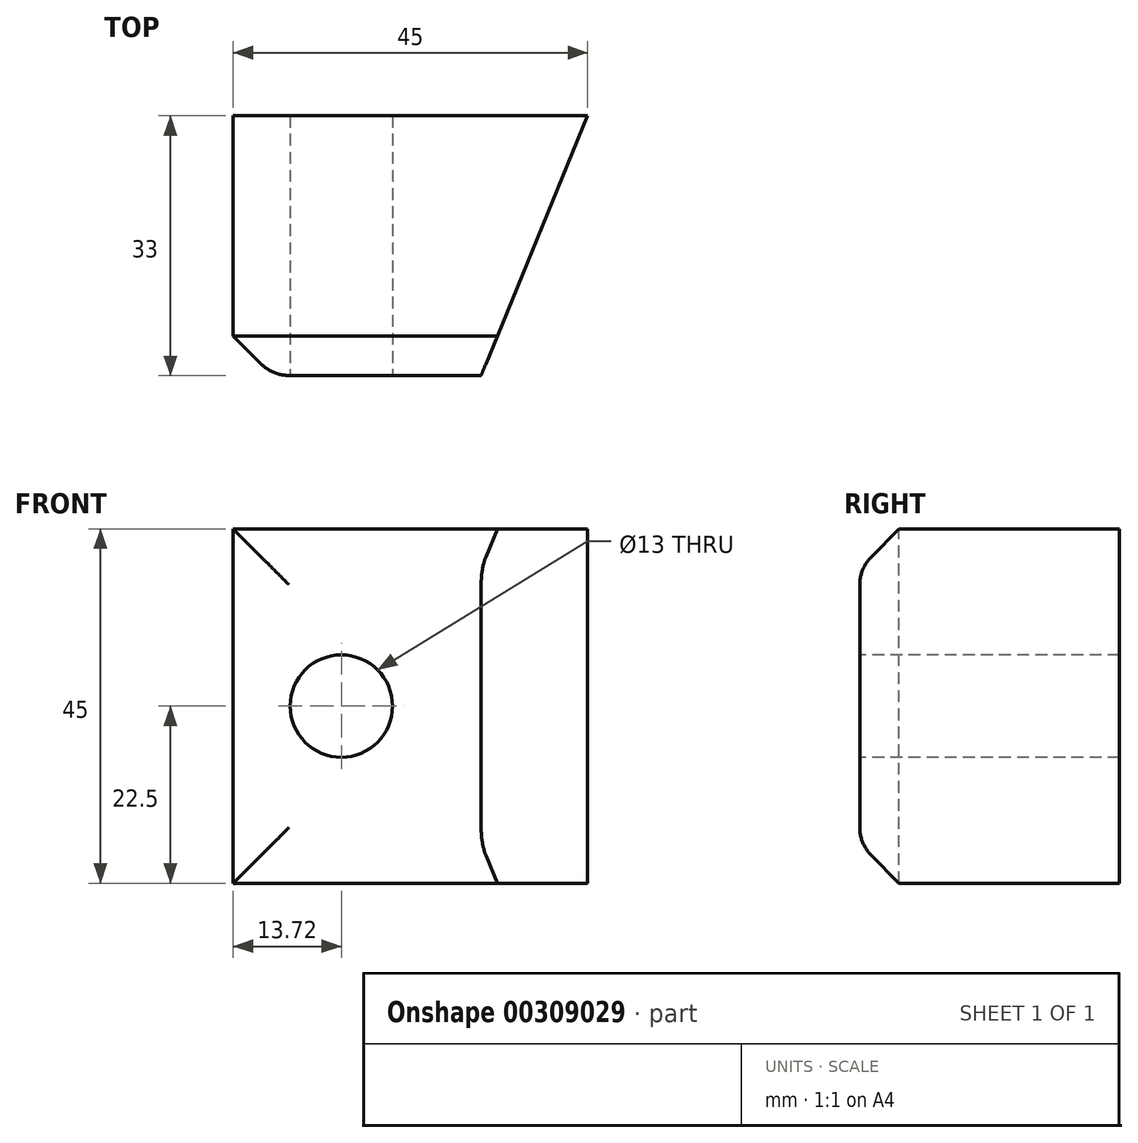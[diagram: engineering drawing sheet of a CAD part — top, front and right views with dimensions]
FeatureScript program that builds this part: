
annotation { "Feature Type Name" : "Feature", "Feature Type Description" : "" }
export const myFeature = defineFeature(function(context is Context, id is Id, definition is map)
    precondition{}
    {
        {
            var Q0;
            Q0=qCreatedBy(makeId("Front.planeOp"),FACE);
            var sketch = newSketch(context, id + "F0", { "sketchPlane" : qUnion([Q0])});
            skLineSegment(sketch, "E0.bottom", {"start": v(22.5, 22.5) * mm, "end": v(-22.5, 22.5) * mm});
            skLineSegment(sketch, "E0.top", {"start": v(22.5, -22.5) * mm, "end": v(-22.5, -22.5) * mm});
            skLineSegment(sketch, "E0.left", {"start": v(22.5, 22.5) * mm, "end": v(22.5, -22.5) * mm});
            skLineSegment(sketch, "E0.right", {"start": v(-22.5, 22.5) * mm, "end": v(-22.5, -22.5) * mm});
            skPoint(sketch, "E0.middle", {"position": v(0, 0) * mm});
            skSolve(sketch);
        }
        {
            var Q0;
            Q0 = qSketchRegion(id + "F0", true);
            extrude(context, id + "F1", {"entities" : qUnion([Q0]), "depth" : 33 * mm, "offsetDistance" : 25 * mm});
        }
        {
            var Q0;
            Q0=makeQuery(id+"F1.opExtrude","SWEPT_FACE",FACE,{"disambiguationData":[OSD([sQuery(id+"F0.wireOp",EDGE,"E0.bottom")])]});
            var sketch = newSketch(context, id + "F2", { "sketchPlane" : qUnion([Q0])});
            skLineSegment(sketch, "E1", {"start": v(22.5, 0) * mm, "end": v(8.98, -33) * mm});
            skLineSegment(sketch, "E2", {"start": v(8.98, -33) * mm, "end": v(22.5, -33) * mm});
            skLineSegment(sketch, "E3", {"start": v(22.5, -33) * mm, "end": v(22.5, 0) * mm});
            skSolve(sketch);
        }
        {
            var Q0;
            Q0 = qSketchRegion(id + "F2", true);
            extrude(context, id + "F3", {"entities" : qUnion([Q0]), "operationType" : NewBodyOperationType.REMOVE, "oppositeDirection" : true, "depth" : 55.8 * mm, "offsetDistance" : 25 * mm});
        }
        {
            var Q0;
            Q0=makeQuery(id+"F1.opExtrude","CAP_FACE",FACE,{"disambiguationData":[OSD([sQuery(id+"F0.wireOp",EDGE,"E0.bottom"),sQuery(id+"F0.wireOp",EDGE,"E0.top"),sQuery(id+"F0.wireOp",EDGE,"E0.left"),sQuery(id+"F0.wireOp",EDGE,"E0.right")])],"isStart":false});
            var sketch = newSketch(context, id + "F4", { "sketchPlane" : qUnion([Q0])});
            skCircle(sketch, "E4", {"center": v(-8.78, 0) * mm, "radius": 6.5 * mm});
            skSolve(sketch);
        }
        {
            var Q0;
            Q0 = qSketchRegion(id + "F4", true);
            extrude(context, id + "F5", {"entities" : qUnion([Q0]), "operationType" : NewBodyOperationType.REMOVE, "oppositeDirection" : true, "depth" : 68.3 * mm, "offsetDistance" : 25 * mm});
        }
        {
            var Q0;
            Q0=makeQuery(id+"F1.opExtrude","CAP_EDGE",EDGE,{"disambiguationData":[OSD([sQuery(id+"F0.wireOp",EDGE,"E0.bottom")])],"isStart":false});
            var Q1;
            Q1=makeQuery(id+"F3.boolean.opBoolean","COPY",EDGE,{"derivedFrom":makeQuery(id+"F3.opExtrude","SWEPT_EDGE",EDGE,{"disambiguationData":[OSD([sQuery(id+"F0.wireOp",EDGE,"E0.bottom"),sQuery(id+"F2.wireOp",EDGE,"E1"),sQuery(id+"F2.wireOp",EDGE,"E2")])]})});
            var Q2;
            Q2=makeQuery(id+"F1.opExtrude","CAP_EDGE",EDGE,{"disambiguationData":[OSD([sQuery(id+"F0.wireOp",EDGE,"E0.top")])],"isStart":false});
            var Q3;
            Q3=makeQuery(id+"F1.opExtrude","CAP_EDGE",EDGE,{"disambiguationData":[OSD([sQuery(id+"F0.wireOp",EDGE,"E0.right")])],"isStart":false});
            chamfer(context, id + "F6", {"entities" : qUnion([Q0, Q1, Q2, Q3]), "width" : 5 * mm, "tangentPropagation" : true});
        }
        {
            var Q0;
            {var subQ0=sQuery(id+"F0.wireOp",EDGE,"E0.bottom");Q0=makeQuery(id+"F6.opChamfer","BLEND_EDGE",EDGE,{"blendedFrom":[makeQuery(id+"F1.opExtrude","CAP_EDGE",EDGE,{"disambiguationData":[OSD([subQ0])],"isStart":false}),makeQuery(id+"F1.opExtrude","CAP_FACE",FACE,{"disambiguationData":[OSD([subQ0,sQuery(id+"F0.wireOp",EDGE,"E0.top"),sQuery(id+"F0.wireOp",EDGE,"E0.left"),sQuery(id+"F0.wireOp",EDGE,"E0.right")])],"isStart":false})],"blendedInto":[makeQuery(id+"F1.opExtrude","CAP_FACE",FACE,{"disambiguationData":[OSD([subQ0,sQuery(id+"F0.wireOp",EDGE,"E0.top"),sQuery(id+"F0.wireOp",EDGE,"E0.left"),sQuery(id+"F0.wireOp",EDGE,"E0.right")])],"isStart":false})]});}
            var Q1;
            {var subQ0=sQuery(id+"F0.wireOp",EDGE,"E0.bottom");Q1=makeQuery(id+"F6.opChamfer","BLEND_EDGE",EDGE,{"blendedFrom":[makeQuery(id+"F3.boolean.opBoolean","COPY",EDGE,{"derivedFrom":makeQuery(id+"F3.opExtrude","SWEPT_EDGE",EDGE,{"disambiguationData":[OSD([subQ0,sQuery(id+"F2.wireOp",EDGE,"E1"),sQuery(id+"F2.wireOp",EDGE,"E2")])]})}),makeQuery(id+"F1.opExtrude","CAP_FACE",FACE,{"disambiguationData":[OSD([subQ0,sQuery(id+"F0.wireOp",EDGE,"E0.top"),sQuery(id+"F0.wireOp",EDGE,"E0.left"),sQuery(id+"F0.wireOp",EDGE,"E0.right")])],"isStart":false})],"blendedInto":[makeQuery(id+"F1.opExtrude","CAP_FACE",FACE,{"disambiguationData":[OSD([subQ0,sQuery(id+"F0.wireOp",EDGE,"E0.top"),sQuery(id+"F0.wireOp",EDGE,"E0.left"),sQuery(id+"F0.wireOp",EDGE,"E0.right")])],"isStart":false})]});}
            var Q2;
            {var subQ0=sQuery(id+"F0.wireOp",EDGE,"E0.top");Q2=makeQuery(id+"F6.opChamfer","BLEND_EDGE",EDGE,{"blendedFrom":[makeQuery(id+"F1.opExtrude","CAP_EDGE",EDGE,{"disambiguationData":[OSD([subQ0])],"isStart":false}),makeQuery(id+"F1.opExtrude","CAP_FACE",FACE,{"disambiguationData":[OSD([sQuery(id+"F0.wireOp",EDGE,"E0.bottom"),subQ0,sQuery(id+"F0.wireOp",EDGE,"E0.left"),sQuery(id+"F0.wireOp",EDGE,"E0.right")])],"isStart":false})],"blendedInto":[makeQuery(id+"F1.opExtrude","CAP_FACE",FACE,{"disambiguationData":[OSD([sQuery(id+"F0.wireOp",EDGE,"E0.bottom"),subQ0,sQuery(id+"F0.wireOp",EDGE,"E0.left"),sQuery(id+"F0.wireOp",EDGE,"E0.right")])],"isStart":false})]});}
            var Q3;
            {var subQ0=sQuery(id+"F0.wireOp",EDGE,"E0.right");Q3=makeQuery(id+"F6.opChamfer","BLEND_EDGE",EDGE,{"blendedFrom":[makeQuery(id+"F1.opExtrude","CAP_EDGE",EDGE,{"disambiguationData":[OSD([subQ0])],"isStart":false}),makeQuery(id+"F1.opExtrude","CAP_FACE",FACE,{"disambiguationData":[OSD([sQuery(id+"F0.wireOp",EDGE,"E0.bottom"),sQuery(id+"F0.wireOp",EDGE,"E0.top"),sQuery(id+"F0.wireOp",EDGE,"E0.left"),subQ0])],"isStart":false})],"blendedInto":[makeQuery(id+"F1.opExtrude","CAP_FACE",FACE,{"disambiguationData":[OSD([sQuery(id+"F0.wireOp",EDGE,"E0.bottom"),sQuery(id+"F0.wireOp",EDGE,"E0.top"),sQuery(id+"F0.wireOp",EDGE,"E0.left"),subQ0])],"isStart":false})]});}
            fillet(context, id + "F7", {"entities" : qUnion([Q0, Q1, Q2, Q3]), "tangentPropagation" : true, "radius" : 5 * mm, "defaultsChanged" : false, "vertexSettings" : [], "allowEdgeOverflow" : false});
        }
    });
